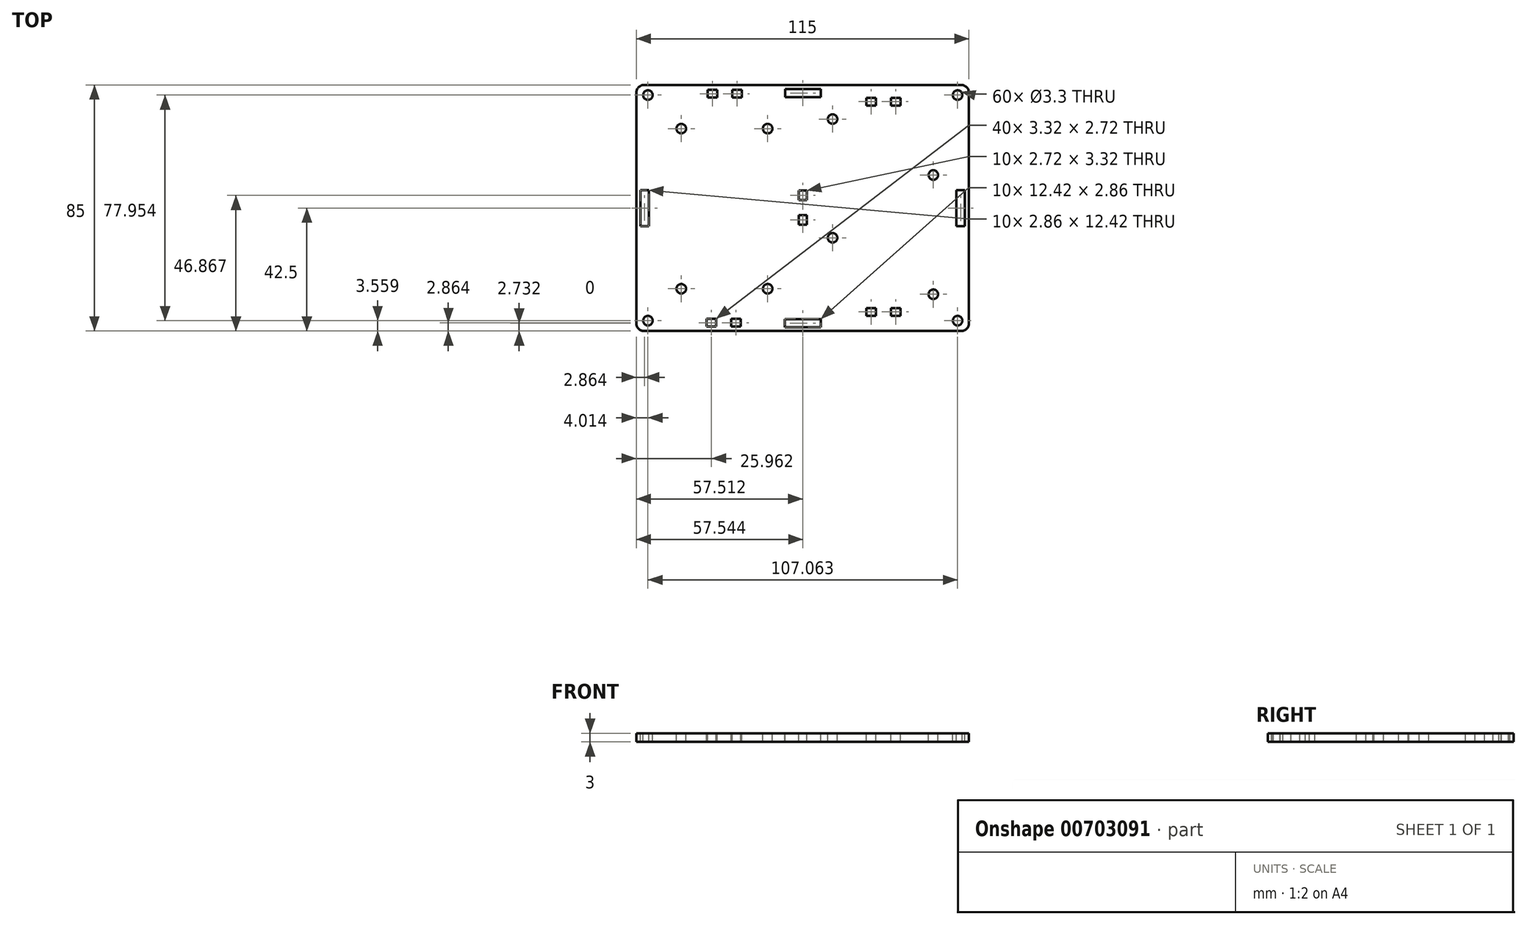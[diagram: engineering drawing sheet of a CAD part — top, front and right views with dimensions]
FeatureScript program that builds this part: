
annotation { "Feature Type Name" : "Feature", "Feature Type Description" : "" }
export const myFeature = defineFeature(function(context is Context, id is Id, definition is map)
    precondition{}
    {
        {
            var Q0;
            Q0=qCreatedBy(makeId("Top.planeOp"),FACE);
            var sketch = newSketch(context, id + "F0", { "sketchPlane" : qUnion([Q0])});
            skLineSegment(sketch, "E0.bottom", {"start": v(57.5, -42.5) * mm, "end": v(-57.5, -42.5) * mm});
            skLineSegment(sketch, "E0.top", {"start": v(57.5, 42.5) * mm, "end": v(-57.5, 42.5) * mm});
            skLineSegment(sketch, "E0.left", {"start": v(57.5, -42.5) * mm, "end": v(57.5, 42.5) * mm});
            skLineSegment(sketch, "E0.right", {"start": v(-57.5, -42.5) * mm, "end": v(-57.5, 42.5) * mm});
            skPoint(sketch, "E0.middle", {"position": v(0, 0) * mm});
            skPoint(sketch, "E1", {"position": v(-53.49, 39.01) * mm});
            skPoint(sketch, "E2", {"position": v(-53.49, -38.94) * mm});
            skPoint(sketch, "E3", {"position": v(53.58, -38.94) * mm});
            skPoint(sketch, "E4", {"position": v(53.58, 39.01) * mm});
            skLineSegment(sketch, "E5.bottom", {"start": v(-53.2, -6.21) * mm, "end": v(-56.06, -6.21) * mm});
            skLineSegment(sketch, "E5.top", {"start": v(-53.2, 6.21) * mm, "end": v(-56.06, 6.21) * mm});
            skLineSegment(sketch, "E5.left", {"start": v(-53.2, -6.21) * mm, "end": v(-53.2, 6.21) * mm});
            skLineSegment(sketch, "E5.right", {"start": v(-56.06, -6.21) * mm, "end": v(-56.06, 6.21) * mm});
            skPoint(sketch, "E5.middle", {"position": v(-54.64, 0) * mm});
            skLineSegment(sketch, "E6.MirrorCS", {"start": v(-53.2, 6.21) * mm, "end": v(-53.2, -6.21) * mm});
            skLineSegment(sketch, "E7.MirrorCS", {"start": v(-56.06, 6.21) * mm, "end": v(-56.06, -6.21) * mm});
            skLineSegment(sketch, "E8.bottom", {"start": v(56.04, -6.26) * mm, "end": v(53.19, -6.26) * mm});
            skLineSegment(sketch, "E8.top", {"start": v(56.04, 6.17) * mm, "end": v(53.19, 6.17) * mm});
            skLineSegment(sketch, "E8.left", {"start": v(56.04, -6.26) * mm, "end": v(56.04, 6.17) * mm});
            skLineSegment(sketch, "E8.right", {"start": v(53.19, -6.26) * mm, "end": v(53.19, 6.17) * mm});
            skPoint(sketch, "E8.middle", {"position": v(54.61, -0.05) * mm});
            skLineSegment(sketch, "E9.MirrorCS", {"start": v(56.04, 6.17) * mm, "end": v(56.04, -6.26) * mm});
            skLineSegment(sketch, "E10.MirrorCS", {"start": v(53.19, 6.17) * mm, "end": v(53.19, -6.26) * mm});
            skPoint(sketch, "E11", {"position": v(-41.95, 27.44) * mm});
            skPoint(sketch, "E12", {"position": v(-12.09, 27.44) * mm});
            skPoint(sketch, "E13", {"position": v(-12.09, -27.9) * mm});
            skPoint(sketch, "E14", {"position": v(-41.95, -27.9) * mm});
            skPoint(sketch, "E15", {"position": v(10.34, -10.3) * mm});
            skPoint(sketch, "E16", {"position": v(45.18, -29.82) * mm});
            skPoint(sketch, "E17", {"position": v(45.18, 11.4) * mm});
            skPoint(sketch, "E18", {"position": v(10.34, 30.74) * mm});
            skLineSegment(sketch, "E19.bottom", {"start": v(-6.2, -41.2) * mm, "end": v(-6.2, -38.34) * mm});
            skLineSegment(sketch, "E19.top", {"start": v(6.22, -41.2) * mm, "end": v(6.22, -38.34) * mm});
            skLineSegment(sketch, "E19.left", {"start": v(-6.2, -41.2) * mm, "end": v(6.22, -41.2) * mm});
            skLineSegment(sketch, "E19.right", {"start": v(-6.2, -38.34) * mm, "end": v(6.22, -38.34) * mm});
            skPoint(sketch, "E19.middle", {"position": v(0.01, -39.77) * mm});
            skLineSegment(sketch, "E20.MirrorCS", {"start": v(6.22, -41.2) * mm, "end": v(-6.2, -41.2) * mm});
            skLineSegment(sketch, "E21.MirrorCS", {"start": v(6.22, -38.34) * mm, "end": v(-6.2, -38.34) * mm});
            skLineSegment(sketch, "E22.bottom", {"start": v(-6.1, 38.3) * mm, "end": v(-6.1, 41.16) * mm});
            skLineSegment(sketch, "E22.top", {"start": v(6.32, 38.3) * mm, "end": v(6.32, 41.16) * mm});
            skLineSegment(sketch, "E22.left", {"start": v(-6.1, 38.3) * mm, "end": v(6.32, 38.3) * mm});
            skLineSegment(sketch, "E22.right", {"start": v(-6.1, 41.16) * mm, "end": v(6.32, 41.16) * mm});
            skPoint(sketch, "E22.middle", {"position": v(0.11, 39.73) * mm});
            skLineSegment(sketch, "E23.MirrorCS", {"start": v(6.32, 38.3) * mm, "end": v(-6.1, 38.3) * mm});
            skLineSegment(sketch, "E24.MirrorCS", {"start": v(6.32, 41.16) * mm, "end": v(-6.1, 41.16) * mm});
            skLineSegment(sketch, "E25.bottom", {"start": v(-1.32, 2.7) * mm, "end": v(1.4, 2.7) * mm});
            skLineSegment(sketch, "E25.top", {"start": v(-1.32, 6.03) * mm, "end": v(1.4, 6.03) * mm});
            skLineSegment(sketch, "E25.left", {"start": v(-1.32, 2.7) * mm, "end": v(-1.32, 6.03) * mm});
            skLineSegment(sketch, "E25.right", {"start": v(1.4, 2.7) * mm, "end": v(1.4, 6.03) * mm});
            skLineSegment(sketch, "E26.bottom", {"start": v(-1.3, -5.8) * mm, "end": v(1.42, -5.8) * mm});
            skLineSegment(sketch, "E26.top", {"start": v(-1.3, -2.48) * mm, "end": v(1.42, -2.48) * mm});
            skLineSegment(sketch, "E26.left", {"start": v(-1.3, -5.8) * mm, "end": v(-1.3, -2.48) * mm});
            skLineSegment(sketch, "E26.right", {"start": v(1.42, -5.8) * mm, "end": v(1.42, -2.48) * mm});
            skLineSegment(sketch, "E27.bottom", {"start": v(-29.5, 38.13) * mm, "end": v(-29.5, 40.85) * mm});
            skLineSegment(sketch, "E27.top", {"start": v(-32.83, 38.13) * mm, "end": v(-32.83, 40.85) * mm});
            skLineSegment(sketch, "E27.left", {"start": v(-29.5, 38.13) * mm, "end": v(-32.83, 38.13) * mm});
            skLineSegment(sketch, "E27.right", {"start": v(-29.5, 40.85) * mm, "end": v(-32.83, 40.85) * mm});
            skLineSegment(sketch, "E28.bottom", {"start": v(-21, 38.15) * mm, "end": v(-21, 40.87) * mm});
            skLineSegment(sketch, "E28.top", {"start": v(-24.32, 38.15) * mm, "end": v(-24.32, 40.87) * mm});
            skLineSegment(sketch, "E28.left", {"start": v(-21, 38.15) * mm, "end": v(-24.32, 38.15) * mm});
            skLineSegment(sketch, "E28.right", {"start": v(-21, 40.87) * mm, "end": v(-24.32, 40.87) * mm});
            skLineSegment(sketch, "E29.bottom", {"start": v(-24.7, -38.26) * mm, "end": v(-24.7, -40.98) * mm});
            skLineSegment(sketch, "E29.top", {"start": v(-21.37, -38.26) * mm, "end": v(-21.37, -40.98) * mm});
            skLineSegment(sketch, "E29.left", {"start": v(-24.7, -38.26) * mm, "end": v(-21.37, -38.26) * mm});
            skLineSegment(sketch, "E29.right", {"start": v(-24.7, -40.98) * mm, "end": v(-21.37, -40.98) * mm});
            skLineSegment(sketch, "E30.bottom", {"start": v(-33.2, -38.28) * mm, "end": v(-33.2, -41) * mm});
            skLineSegment(sketch, "E30.top", {"start": v(-29.88, -38.28) * mm, "end": v(-29.88, -41) * mm});
            skLineSegment(sketch, "E30.left", {"start": v(-33.2, -38.28) * mm, "end": v(-29.88, -38.28) * mm});
            skLineSegment(sketch, "E30.right", {"start": v(-33.2, -41) * mm, "end": v(-29.88, -41) * mm});
            skPoint(sketch, "E31.startSnap0", {"position": v(27.88, -20.23) * mm});
            skLineSegment(sketch, "E32.bottom", {"start": v(25.38, -37.29) * mm, "end": v(25.38, -34.57) * mm});
            skLineSegment(sketch, "E32.top", {"start": v(22.06, -37.29) * mm, "end": v(22.06, -34.57) * mm});
            skLineSegment(sketch, "E32.left", {"start": v(25.38, -37.29) * mm, "end": v(22.06, -37.29) * mm});
            skLineSegment(sketch, "E32.right", {"start": v(25.38, -34.57) * mm, "end": v(22.06, -34.57) * mm});
            skLineSegment(sketch, "E33.bottom", {"start": v(33.9, -37.27) * mm, "end": v(33.9, -34.55) * mm});
            skLineSegment(sketch, "E33.top", {"start": v(30.57, -37.27) * mm, "end": v(30.57, -34.55) * mm});
            skLineSegment(sketch, "E33.left", {"start": v(33.9, -37.27) * mm, "end": v(30.57, -37.27) * mm});
            skLineSegment(sketch, "E33.right", {"start": v(33.9, -34.55) * mm, "end": v(30.57, -34.55) * mm});
            skLineSegment(sketch, "E34.bottom", {"start": v(25.33, 35.36) * mm, "end": v(25.33, 38.08) * mm});
            skLineSegment(sketch, "E34.top", {"start": v(22.01, 35.36) * mm, "end": v(22.01, 38.08) * mm});
            skLineSegment(sketch, "E34.left", {"start": v(25.33, 35.36) * mm, "end": v(22.01, 35.36) * mm});
            skLineSegment(sketch, "E34.right", {"start": v(25.33, 38.08) * mm, "end": v(22.01, 38.08) * mm});
            skLineSegment(sketch, "E35.bottom", {"start": v(33.84, 35.38) * mm, "end": v(33.84, 38.1) * mm});
            skLineSegment(sketch, "E35.top", {"start": v(30.52, 35.38) * mm, "end": v(30.52, 38.1) * mm});
            skLineSegment(sketch, "E35.left", {"start": v(33.84, 35.38) * mm, "end": v(30.52, 35.38) * mm});
            skLineSegment(sketch, "E35.right", {"start": v(33.84, 38.1) * mm, "end": v(30.52, 38.1) * mm});
            skSolve(sketch);
        }
        {
            var Q0;
            Q0=makeQuery(id+"F0.imprint","IMPRINT",FACE,{"disambiguationData":[TD([[makeQuery(id+"F0.imprint","IMPRINT",EDGE,{"derivedFrom":sQuery(id+"F0.wireOp",EDGE,"E0.bottom")}),-1.0]])]});
            extrude(context, id + "F1", {"entities" : qUnion([Q0]), "oppositeDirection" : true, "depth" : 3 * mm, "offsetDistance" : 25 * mm});
        }
        {
            var Q0;
            Q0=makeQuery(id+"F1.opExtrude","SWEPT_EDGE",EDGE,{"disambiguationData":[OSD([sQuery(id+"F0.wireOp",EDGE,"E0.bottom"),sQuery(id+"F0.wireOp",EDGE,"E0.left")])]});
            var Q1;
            Q1=makeQuery(id+"F1.opExtrude","SWEPT_EDGE",EDGE,{"disambiguationData":[OSD([sQuery(id+"F0.wireOp",EDGE,"E0.top"),sQuery(id+"F0.wireOp",EDGE,"E0.left")])]});
            var Q2;
            Q2=makeQuery(id+"F1.opExtrude","SWEPT_EDGE",EDGE,{"disambiguationData":[OSD([sQuery(id+"F0.wireOp",EDGE,"E0.bottom"),sQuery(id+"F0.wireOp",EDGE,"E0.right")])]});
            var Q3;
            Q3=makeQuery(id+"F1.opExtrude","SWEPT_EDGE",EDGE,{"disambiguationData":[OSD([sQuery(id+"F0.wireOp",EDGE,"E0.top"),sQuery(id+"F0.wireOp",EDGE,"E0.right")])]});
            fillet(context, id + "F2", {"entities" : qUnion([Q0, Q1, Q2, Q3]), "radius" : 2.66 * mm, "tangentPropagation" : true, "allowEdgeOverflow" : false});
        }
        {
            var Q0;
            Q0=sQuery(id+"F0.wireOp",VERTEX,"E2");
            var Q1;
            Q1=sQuery(id+"F0.wireOp",VERTEX,"E1");
            var Q2;
            Q2=sQuery(id+"F0.wireOp",VERTEX,"E3");
            var Q3;
            Q3=sQuery(id+"F0.wireOp",VERTEX,"E4");
            var Q4;
            Q4=makeQuery(id+"F1.opExtrude","SWEPT_BODY",BODY,{"disambiguationData":[OSD([sQuery(id+"F0.wireOp",EDGE,"E0.bottom"),sQuery(id+"F0.wireOp",EDGE,"E0.top"),sQuery(id+"F0.wireOp",EDGE,"E0.left"),sQuery(id+"F0.wireOp",EDGE,"E0.right")])]});
            hole(context, id + "F3", {"style" : HoleStyle.SIMPLE, "endStyle" : HoleEndStyle.BLIND, "standardTappedOrClearance" : lookupTablePath({ "standard" : "ISO", "fit" : "Normal", "size" : "M3", "type" : "Clearance" }), "standardBlindInLast" : lookupTablePath({ "fit" : "Standard", "standard" : "ISO", "size" : "M3", "type" : "Clearance" }), "holeDiameter" : 3.3 * mm, "majorDiameter" : 3 * mm, "holeDepth" : 13.5 * mm, "isTappedThrough" : true, "tappedDepth" : 12 * mm, "tapClearance" : 3, "locations" : qUnion([Q0, Q1, Q2, Q3]), "scope" : qUnion([Q4])});
        }
        {
            var Q0;
            Q0=sQuery(id+"F0.wireOp",VERTEX,"E11");
            var Q1;
            Q1=sQuery(id+"F0.wireOp",VERTEX,"E12");
            var Q2;
            Q2=sQuery(id+"F0.wireOp",VERTEX,"E13");
            var Q3;
            Q3=sQuery(id+"F0.wireOp",VERTEX,"E18");
            var Q4;
            Q4=sQuery(id+"F0.wireOp",VERTEX,"E17");
            var Q5;
            Q5=sQuery(id+"F0.wireOp",VERTEX,"E16");
            var Q6;
            Q6=sQuery(id+"F0.wireOp",VERTEX,"E15");
            var Q7;
            Q7=sQuery(id+"F0.wireOp",VERTEX,"E14");
            var Q8;
            Q8=makeQuery(id+"F1.opExtrude","SWEPT_BODY",BODY,{"disambiguationData":[OSD([sQuery(id+"F0.wireOp",EDGE,"E0.bottom"),sQuery(id+"F0.wireOp",EDGE,"E0.top"),sQuery(id+"F0.wireOp",EDGE,"E0.left"),sQuery(id+"F0.wireOp",EDGE,"E0.right"),sQuery(id+"F0.wireOp",EDGE,"E5.bottom"),sQuery(id+"F0.wireOp",EDGE,"E5.top"),sQuery(id+"F0.wireOp",EDGE,"E6.MirrorCS"),sQuery(id+"F0.wireOp",EDGE,"E7.MirrorCS"),sQuery(id+"F0.wireOp",EDGE,"E8.bottom"),sQuery(id+"F0.wireOp",EDGE,"E8.top"),sQuery(id+"F0.wireOp",EDGE,"E9.MirrorCS"),sQuery(id+"F0.wireOp",EDGE,"E10.MirrorCS")])]});
            hole(context, id + "F4", {"style" : HoleStyle.SIMPLE, "endStyle" : HoleEndStyle.THROUGH, "standardTappedOrClearance" : lookupTablePath({ "standard" : "ISO", "fit" : "Normal", "size" : "M3", "type" : "Clearance" }), "standardBlindInLast" : lookupTablePath({ "fit" : "Standard", "standard" : "ISO", "size" : "M3", "type" : "Clearance" }), "holeDiameter" : 3.3 * mm, "majorDiameter" : 5 * mm, "isTappedThrough" : true, "tappedDepth" : 12 * mm, "tapClearance" : 3, "startFromSketch" : true, "locations" : qUnion([Q0, Q1, Q2, Q3, Q4, Q5, Q6, Q7]), "scope" : qUnion([Q8])});
        }
    });
